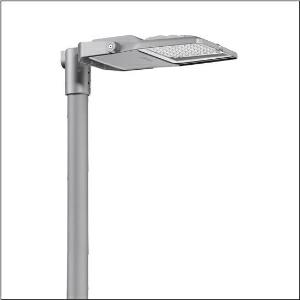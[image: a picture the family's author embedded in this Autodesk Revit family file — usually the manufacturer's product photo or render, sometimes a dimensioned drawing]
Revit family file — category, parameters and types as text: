
# Revit family: floodlight_fl_21_mini___pl61_5xa7775d2c3a_f3a4
name_source: partatom
category: Lighting Fixtures
units: mm (PartAtom-declared; Revit-internal decimal feet)

## family parameters
Cut with Voids When Loaded = No
Host = Face
Light Source = No
Part Type = Normal
Room Calculation Point = No
Round Connector Dimension = Use Diameter
Shared = No

## types (1)
- --- (1 x LED, 17510 lm, 142.9 W, 3000K)
    Apparent Load = 143 VA
    CIE Flux Codes = 33 65 98 100 100
    Color Rendering = 70
    Color Temperature = 3000K
    Default Elevation = 1800 mm
    Description = Floodlight FL 21 mini, floodlight, primary light control with lens, of PMMA, primary optical cover: protective disc, of toughened safety glass, transparent, light distribution: PL61, light emission: direct distribution, installation type: surface-mounted, LED, High Power LED, rated luminous flux: 17.510lm, luminous efficacy: 123lm/W, light colour: 730, colour temperature: 3000K, control: flexible luminous flux parameterisation, time-dependent luminous flux control, constant luminous flux control, overheat protection, presetting dimming logarithmic, with terminal, 6-pole, mains connection: 220..240V, AC, 50/60Hz, start of lifetime: 143W, end of service life: 151W, reduction: 63W, luminaire housing, of diecast aluminium, powder-coated, Siteco® metallic grey (DB 702S), corrosivity category C5 mid according to DIN EN ISO 12944, sealing non-destructively replaceable, please order mast flange separately, mast bracket, of steel, galvanised, powder-coated, Siteco® metallic grey (DB 702S), Smart Interface above, protection rating (complete): IP66, insulation class (complete): insulation class II (safety insulation), certification: CE, ENEC, VDE, protection symbol: D, impact resistance: IK08, permissible operating ambient temperature: -40..+40°C, permissible operating ambient temperature for outdoor applications: -40..+50°C, standard: DIN EN 12944, LABS conformity tested according to VDMA 24364:2018-05, packaging unit: 1 piece

Light Distribution: PL61
    Height = 70 mm
    Lamp = 1 x LED
    Lamp Light Flux = 17510 lm
    Lamp Power = 142.9 W
    Lamp count = 1
    Length = 485 mm
    Luminous efficacy = 123 lm/W
    Manufacturer = Siteco
    ModVariant = No
    Model = 5XA7775D2C3A
    Number of Poles = 1
    OnlyDefault = Yes
    Power Factor = 1
    Product Name = Floodlight FL 21 mini | PL61
    Product group = floodlight | pylon annexe
    ProductGroupID = 6200
    Protection Class = Protection class II
    Protection Degree = IP 66
    RLX_Detail_Level = 1
    RLX_Emergency_Light_Flux = 0 lm
    RLX_Emergency_Type = 0
    RLX_Emergency_Type_DB = No
    RlxData = <blob elided: 101245 chars, md5=15c92e62>
    Socket = socket
    Standby Power = 0 W
    System Light Flux = 17510 lm
    System Power = 143 W
    Type Comments = factory setting: luminous flux: 100 % | dim-lin: 254 | 730 mA
    Type Image = l_1007125.jpg
    URL = http://relux.com
    VarID = @adj_122853
    Voltage = 0 V
    Weight = 0.00 kg
    Width = 337 mm

## geometry (parser evidence)
native form markers: Blend x4, Sweep x14
no freeform markers — native parametric forms only
